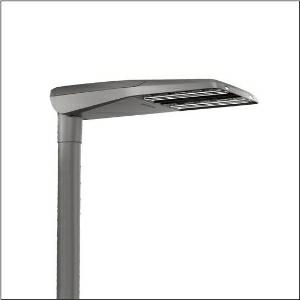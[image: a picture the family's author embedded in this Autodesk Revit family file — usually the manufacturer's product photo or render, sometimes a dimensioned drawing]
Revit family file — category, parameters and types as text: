
# Revit family: streetlight_sl_11_iq_midi___pc-l_5xc3e41f08me_04b4
name_source: partatom
category: Lighting Fixtures
units: mm (PartAtom-declared; Revit-internal decimal feet)

## family parameters
Cut with Voids When Loaded = No
Host = Face
Light Source = No
Part Type = Normal
Room Calculation Point = No
Round Connector Dimension = Use Diameter
Shared = No

## types (1)
- --- (1 x LED, 16220 lm, 124.7 W, 4000K)
    Apparent Load = 125 VA
    CIE Flux Codes = 37 73 96 100 100
    Color Rendering = 70
    Color Temperature = 4000K
    Default Elevation = 1800 mm
    Description = Streetlight SL 11 iQ midi, mast luminaire, primary light control with 3 zone facetted reflector, of plastic, silver coated, highly specular, primary optical cover: cover, of PMMA, transparent, light distribution: PC-L, light emission: direct distribution, primary light characteristic: asymmetric, installation type: post-top, side-entry, LED, High Power LED, rated luminous flux: 16.220lm, luminous efficacy: 130lm/W, light colour: 740, colour temperature: 4000K, control: Street-Remote, optimised constant luminous flux control (CLO 2.0), Desk-Remote (wireless, voltage-free reading and setting of iQ features in the workshop via application-optimized NFC function/RFID function), Light-Fading, Smart-Wire, Night-Set, Lumen-Switch, Temp-Guard, Auto-Match, with cable H07RN-F 5x 1.5mm², mains connection: 220..240V, AC, 50/60Hz, connection cable pre-assembled, cable length: 12,5m, start of lifetime: 125W, end of lifetime: 132W, reduction: 57W, luminaire housing, of diecast aluminium, powder-coated, Siteco® metallic grey (DB 702S), length: 780mm, width: 376mm, height: 118mm, spigot size: 60/76mm (post-top) and 42/60/76mm (side-entry), mast flange for spigot size: 42mm: 5XC10008XM4, 60mm: 5XC10008XM2, 76/60mm: 5XC10108XM1, equipment: Power, protection rating (complete): IP66, insulation class (complete): insulation class II (safety insulation), certification: CE, ENEC, VDE, impact resistance: IK09, permissible operating ambient temperature for outdoor applications: -25..+50°C, standard-compliant lighting for roads and squares, packaging unit: 1 piece

Light Distribution: PC-L
    Height = 118 mm
    Lamp = 1 x LED
    Lamp Light Flux = 16220 lm
    Lamp Power = 124.7 W
    Lamp count = 1
    Length = 780 mm
    Luminous efficacy = 130 lm/W
    Manufacturer = Siteco
    ModVariant = No
    Model = 5XC3E41F08ME
    Number of Poles = 1
    OnlyDefault = Yes
    Power Factor = 1
    Product Name = Streetlight SL 11 iQ midi | PC-L
    Product group = mast luminaire | pylon top
    ProductGroupID = 6100
    Protection Class = Protection class II
    Protection Degree = IP 66
    RLX_Detail_Level = 1
    RlxData = <blob elided: 74349 chars, md5=f75a642c>
    Socket = socket
    Standby Power = 0 W
    System Light Flux = 16220 lm
    System Power = 125 W
    Type Comments = factory setting: luminous flux: 100 % | dim-lin: 254 | 557 mA
    Type Image = l_1005960.jpg
    URL = http://relux.com
    VarID = @adj_118007
    Voltage = 0 V
    Weight = 0.00 kg
    Width = 376 mm

## geometry (parser evidence)
native form markers: Blend x4, Sweep x11
no freeform markers — native parametric forms only
